annotation { "Feature Type Name" : "Feature", "Feature Type Description" : "" }
export const myFeature = defineFeature(function(context is Context, id is Id, definition is map)
    precondition{}
    {
        {
            var Q0;
            Q0=qCreatedBy(makeId("Top.planeOp"),FACE);
            var sketch = newSketch(context, id + "F0", { "sketchPlane" : qUnion([Q0])});
            skLineSegment(sketch, "E0.bottom", {"start": v(-43.83, 34.62) * mm, "end": v(22.17, 34.62) * mm});
            skLineSegment(sketch, "E0.top", {"start": v(-42.5, -18.38) * mm, "end": v(22.17, -18.38) * mm});
            skLineSegment(sketch, "E0.left", {"start": v(-43.83, 34.62) * mm, "end": v(-43.83, 32.11) * mm});
            skLineSegment(sketch, "E0.right", {"start": v(22.17, 34.62) * mm, "end": v(22.17, -18.38) * mm});
            skLineSegment(sketch, "E1", {"start": v(-43.83, -16.89) * mm, "end": v(-42.5, -18.38) * mm});
            skLineSegment(sketch, "E2.right", {"start": v(-46.83, 29.1) * mm, "end": v(-46.73, -3) * mm});
            skLineSegment(sketch, "E3", {"start": v(-43.83, 32.11) * mm, "end": v(-46.83, 29.1) * mm});
            skLineSegment(sketch, "E4", {"start": v(-46.73, -3) * mm, "end": v(-43.83, -5.89) * mm});
            skLineSegment(sketch, "E5.trimOffspring", {"start": v(-43.83, -5.89) * mm, "end": v(-43.83, -16.89) * mm});
            skCircle(sketch, "E6", {"center": v(-44.33, 27.39) * mm, "radius": 2.25 * mm});
            skCircle(sketch, "E7", {"center": v(-44.24, -1.2) * mm, "radius": 2.25 * mm});
            skCircle(sketch, "E8", {"center": v(6.92, 32.12) * mm, "radius": 2.25 * mm});
            skCircle(sketch, "E9", {"center": v(6.92, -15.88) * mm, "radius": 2.25 * mm});
            skSolve(sketch);
        }
        {
            var Q0;
            Q0=makeQuery(id+"F0.imprint","IMPRINT",FACE,{"disambiguationData":[TD([[makeQuery(id+"F0.imprint","IMPRINT",EDGE,{"derivedFrom":sQuery(id+"F0.wireOp",EDGE,"E0.bottom")}),-1.0]])]});
            var Q1;
            Q1=makeQuery(id+"F0.imprint","IMPRINT",FACE,{"disambiguationData":[TD([[makeQuery(id+"F0.imprint","IMPRINT",EDGE,{"derivedFrom":sQuery(id+"F0.wireOp",EDGE,"oReomVxt-EG6t-q1BH-AZSM-6wqQi52AqEO8")}),-1.0]])]});
            extrude(context, id + "F1", {"entities" : qUnion([Q0, Q1]), "depth" : 1 * mm});
        }
        {
            var Q0;
            Q0=makeQuery(id+"F1.opExtrude","CAP_FACE",FACE,{"disambiguationData":[OSD([sQuery(id+"F0.wireOp",EDGE,"E0.bottom"),sQuery(id+"F0.wireOp",EDGE,"E0.top"),sQuery(id+"F0.wireOp",EDGE,"E0.left"),sQuery(id+"F0.wireOp",EDGE,"E0.right"),sQuery(id+"F0.wireOp",EDGE,"E1"),sQuery(id+"F0.wireOp",EDGE,"E2.right"),sQuery(id+"F0.wireOp",EDGE,"E3"),sQuery(id+"F0.wireOp",EDGE,"E4"),sQuery(id+"F0.wireOp",EDGE,"E5.trimOffspring"),sQuery(id+"F0.wireOp",EDGE,"E6"),sQuery(id+"F0.wireOp",EDGE,"E7"),sQuery(id+"F0.wireOp",EDGE,"E8"),sQuery(id+"F0.wireOp",EDGE,"E9")])],"isStart":true});
            var sketch = newSketch(context, id + "F2", { "sketchPlane" : qUnion([Q0])});
            skText(sketch, "E10", { "text": "Seonwoo Cho\nJulia Angel", "fontName": "OpenSans-Regular.ttf"});
            const initialGuessF2  = {"E10": [-0.03303, 0.00577, 1, 0, 0.006]};
            skSetInitialGuess(sketch, initialGuessF2);
            skSolve(sketch);
        }
        {
            var Q0;
            Q0=qSketchRegion(id+"F2",true);
            extrude(context, id + "F3", {"entities" : qUnion([Q0]), "operationType" : NewBodyOperationType.REMOVE, "oppositeDirection" : true, "depth" : 0.01 * mm});
        }
        {
            var Q0;
            Q0=makeQuery(id+"F1.opExtrude","CAP_FACE",FACE,{"disambiguationData":[OSD([sQuery(id+"F0.wireOp",EDGE,"E0.bottom"),sQuery(id+"F0.wireOp",EDGE,"E0.top"),sQuery(id+"F0.wireOp",EDGE,"E0.left"),sQuery(id+"F0.wireOp",EDGE,"E0.right"),sQuery(id+"F0.wireOp",EDGE,"E1"),sQuery(id+"F0.wireOp",EDGE,"E2.right"),sQuery(id+"F0.wireOp",EDGE,"E3"),sQuery(id+"F0.wireOp",EDGE,"E4"),sQuery(id+"F0.wireOp",EDGE,"E5.trimOffspring"),sQuery(id+"F0.wireOp",EDGE,"E6"),sQuery(id+"F0.wireOp",EDGE,"E7"),sQuery(id+"F0.wireOp",EDGE,"E8"),sQuery(id+"F0.wireOp",EDGE,"E9")])],"isStart":false});
            var sketch = newSketch(context, id + "F4", { "sketchPlane" : qUnion([Q0])});
            skLineSegment(sketch, "E11.bottom", {"start": v(17.67, -3.38) * mm, "end": v(25.67, -3.38) * mm});
            skLineSegment(sketch, "E11.top", {"start": v(17.67, -10.38) * mm, "end": v(25.67, -10.38) * mm});
            skLineSegment(sketch, "E11.left", {"start": v(17.67, -3.38) * mm, "end": v(17.67, -10.38) * mm});
            skLineSegment(sketch, "E11.right", {"start": v(25.67, -3.38) * mm, "end": v(25.67, -10.38) * mm});
            skSolve(sketch);
        }
        {
            var Q0;
            {var subQ0=sQuery(id+"F4.wireOp",EDGE,"E11.right");Q0=makeQuery(id+"F4.imprint","IMPRINT",FACE,{"disambiguationData":[TD([[makeQuery(id+"F4.imprint","IMPRINT",EDGE,{"derivedFrom":subQ0}),-1.0]])]});}
            var Q1;
            {var subQ0=sQuery(id+"F4.wireOp",EDGE,"E11.left");Q1=makeQuery(id+"F4.imprint","IMPRINT",FACE,{"disambiguationData":[TD([[makeQuery(id+"F4.imprint","IMPRINT",EDGE,{"derivedFrom":subQ0}),1.0]])]});}
            extrude(context, id + "F5", {"entities" : qUnion([Q0, Q1]), "operationType" : NewBodyOperationType.ADD, "depth" : 4 * mm});
        }
        {
            var Q0;
            Q0=makeQuery(id+"F5.opExtrude","SWEPT_FACE",FACE,{"disambiguationData":[OSD([sQuery(id+"F4.wireOp",EDGE,"E11.right")])]});
            var sketch = newSketch(context, id + "F6", { "sketchPlane" : qUnion([Q0])});
            skLineSegment(sketch, "E12", {"start": v(-10.38, 3) * mm, "end": v(-10.11, 2.75) * mm});
            skLineSegment(sketch, "E13", {"start": v(-10.08, 2.67) * mm, "end": v(-10.08, 1) * mm});
            skLineSegment(sketch, "E14", {"start": v(-3.38, 3) * mm, "end": v(-3.65, 2.75) * mm});
            skLineSegment(sketch, "E15", {"start": v(-3.68, 2.68) * mm, "end": v(-3.68, 1) * mm});
            skPoint(sketch, "E16.visualSharp", {"position": v(-3.68, 2.72) * mm});
            skArc(sketch, "E16.filletArc", {"start": v(-3.65, 2.75) * mm, "mid": v(-3.67, 2.72) * mm, "end": v(-3.68, 2.68) * mm});
            skPoint(sketch, "E17.visualSharp", {"position": v(-10.08, 2.72) * mm});
            skArc(sketch, "E17.filletArc", {"start": v(-10.08, 2.67) * mm, "mid": v(-10.09, 2.71) * mm, "end": v(-10.11, 2.75) * mm});
            skArc(sketch, "E18", {"start": v(-10.17, 5) * mm, "mid": v(-10.33, 4.94) * mm, "end": v(-10.38, 4.77) * mm});
            skArc(sketch, "E19", {"start": v(-3.38, 4.86) * mm, "mid": v(-3.44, 4.95) * mm, "end": v(-3.54, 5) * mm});
            skArc(sketch, "E20", {"start": v(-10.08, 1.19) * mm, "mid": v(-10.05, 1.08) * mm, "end": v(-9.98, 1) * mm});
            skArc(sketch, "E21", {"start": v(-3.85, 1) * mm, "mid": v(-3.74, 1.05) * mm, "end": v(-3.68, 1.17) * mm});
            skArc(sketch, "E22", {"start": v(-10.38, 3.04) * mm, "mid": v(-10.38, 3.01) * mm, "end": v(-10.36, 2.98) * mm});
            skArc(sketch, "E23", {"start": v(-3.48, 2.91) * mm, "mid": v(-3.37, 3.02) * mm, "end": v(-3.38, 3.18) * mm});
            skLineSegment(sketch, "E24", {"start": v(-10.08, 4.8) * mm, "end": v(-3.72, 4.8) * mm});
            skLineSegment(sketch, "E25", {"start": v(-3.58, 4.66) * mm, "end": v(-3.57, 3.17) * mm});
            skLineSegment(sketch, "E26", {"start": v(-3.87, 2.75) * mm, "end": v(-3.62, 3.04) * mm});
            skLineSegment(sketch, "E27", {"start": v(-3.87, 1.33) * mm, "end": v(-3.87, 2.75) * mm});
            skLineSegment(sketch, "E28", {"start": v(-10.19, 4.7) * mm, "end": v(-10.19, 3.14) * mm});
            skLineSegment(sketch, "E29", {"start": v(-9.9, 2.75) * mm, "end": v(-9.88, 1.26) * mm});
            skLineSegment(sketch, "E30", {"start": v(-4, 1.19) * mm, "end": v(-9.78, 1.18) * mm});
            skLineSegment(sketch, "E31", {"start": v(-10.13, 2.98) * mm, "end": v(-9.9, 2.75) * mm});
            skArc(sketch, "E32", {"start": v(-3.58, 4.66) * mm, "mid": v(-3.63, 4.75) * mm, "end": v(-3.72, 4.8) * mm});
            skArc(sketch, "E33", {"start": v(-10.08, 4.8) * mm, "mid": v(-10.15, 4.77) * mm, "end": v(-10.19, 4.7) * mm});
            skArc(sketch, "E34", {"start": v(-10.19, 3.14) * mm, "mid": v(-10.17, 3.06) * mm, "end": v(-10.13, 2.98) * mm});
            skArc(sketch, "E35", {"start": v(-9.88, 1.3) * mm, "mid": v(-9.85, 1.21) * mm, "end": v(-9.78, 1.18) * mm});
            skArc(sketch, "E36", {"start": v(-4, 1.19) * mm, "mid": v(-3.9, 1.23) * mm, "end": v(-3.87, 1.33) * mm});
            skArc(sketch, "E37", {"start": v(-3.62, 3.04) * mm, "mid": v(-3.58, 3.1) * mm, "end": v(-3.57, 3.17) * mm});
            skPoint(sketch, "E38.orphan", {"position": v(-10.19, 3.04) * mm});
            skSolve(sketch);
        }
        {
            var Q0;
            {var subQ0=sQuery(id+"F6.wireOp",EDGE,"E14");Q0=makeQuery(id+"F6.imprint","IMPRINT",FACE,{"disambiguationData":[TD([[makeQuery(id+"F6.imprint","IMPRINT",EDGE,{"derivedFrom":subQ0}),1.0]])]});}
            extrude(context, id + "F7", {"entities" : qUnion([Q0]), "operationType" : NewBodyOperationType.REMOVE, "oppositeDirection" : true, "depth" : 25.4 * mm});
        }
        {
            var Q0;
            {var subQ0=sQuery(id+"F6.wireOp",EDGE,"E12");Q0=makeQuery(id+"F6.imprint","IMPRINT",FACE,{"disambiguationData":[TD([[makeQuery(id+"F6.imprint","IMPRINT",EDGE,{"derivedFrom":subQ0}),-1.0]])]});}
            extrude(context, id + "F8", {"entities" : qUnion([Q0]), "operationType" : NewBodyOperationType.REMOVE, "oppositeDirection" : true, "depth" : 25.4 * mm});
        }
        {
            var Q0;
            {var subQ0=sQuery(id+"F4.wireOp",EDGE,"E11.left");Q0=makeQuery(id+"F4.imprint","IMPRINT",FACE,{"disambiguationData":[TD([[makeQuery(id+"F4.imprint","IMPRINT",EDGE,{"derivedFrom":subQ0}),-1.0]])]});}
            var sketch = newSketch(context, id + "F9", { "sketchPlane" : qUnion([Q0])});
            skLineSegment(sketch, "E39", {"start": v(21.67, -10.38) * mm, "end": v(21.67, -3.38) * mm});
            skLineSegment(sketch, "E40", {"start": v(21.67, -3.38) * mm, "end": v(25.67, -3.38) * mm});
            skLineSegment(sketch, "E41", {"start": v(21.67, -10.38) * mm, "end": v(25.67, -10.38) * mm});
            skLineSegment(sketch, "E42.bottom", {"start": v(-42.83, 33.62) * mm, "end": v(-27.33, 33.62) * mm});
            skLineSegment(sketch, "E42.top", {"start": v(-42.83, 31.62) * mm, "end": v(-27.33, 31.62) * mm});
            skLineSegment(sketch, "E42.left", {"start": v(-42.83, 33.62) * mm, "end": v(-42.83, 31.62) * mm});
            skLineSegment(sketch, "E42.right", {"start": v(-27.33, 33.62) * mm, "end": v(-27.33, 31.62) * mm});
            skLineSegment(sketch, "E43.bottom", {"start": v(-25.33, 33.62) * mm, "end": v(-9.83, 33.62) * mm});
            skLineSegment(sketch, "E43.top", {"start": v(-25.33, 31.62) * mm, "end": v(-9.83, 31.62) * mm});
            skLineSegment(sketch, "E43.left", {"start": v(-25.33, 33.62) * mm, "end": v(-25.33, 31.62) * mm});
            skLineSegment(sketch, "E43.right", {"start": v(-9.83, 33.62) * mm, "end": v(-9.83, 31.62) * mm});
            skLineSegment(sketch, "E44.bottom", {"start": v(-42.83, -15.38) * mm, "end": v(-22.33, -15.38) * mm});
            skLineSegment(sketch, "E44.top", {"start": v(-42.83, -17.38) * mm, "end": v(-22.33, -17.38) * mm});
            skLineSegment(sketch, "E44.left", {"start": v(-42.83, -15.38) * mm, "end": v(-42.83, -17.38) * mm});
            skLineSegment(sketch, "E44.right", {"start": v(-22.33, -15.38) * mm, "end": v(-22.33, -17.38) * mm});
            skLineSegment(sketch, "E45.bottom", {"start": v(-20.33, -15.38) * mm, "end": v(0.17, -15.38) * mm});
            skLineSegment(sketch, "E45.top", {"start": v(-20.33, -17.38) * mm, "end": v(0.17, -17.38) * mm});
            skLineSegment(sketch, "E45.left", {"start": v(-20.33, -15.38) * mm, "end": v(-20.33, -17.38) * mm});
            skLineSegment(sketch, "E45.right", {"start": v(0.17, -15.38) * mm, "end": v(0.17, -17.38) * mm});
            skSolve(sketch);
        }
        {
            var Q0;
            {var subQ0=sQuery(id+"F6.wireOp",EDGE,"E19");var subQ1=sQuery(id+"F4.wireOp",EDGE,"E11.right");var subQ4=makeQuery(id+"F5.opExtrude","CAP_EDGE",EDGE,{"disambiguationData":[OSD([subQ1])],"isStart":false});var subQ5=makeQuery(id+"F6.imprint","INTERSECT",VERTEX,{"disambiguationData":[OD(1.0)],"derivedFrom":[subQ4,subQ0]});Q0=makeQuery(id+"F6.imprint","IMPRINT",FACE,{"disambiguationData":[TD([[makeQuery(id+"F6.imprint","IMPRINT",EDGE,{"disambiguationData":[TD([[subQ5,1.0]])],"derivedFrom":subQ0}),-1.0]])]});}
            extrude(context, id + "F10", {"entities" : qUnion([Q0]), "operationType" : NewBodyOperationType.REMOVE, "oppositeDirection" : true, "depth" : 25.4 * mm});
        }
        {
            var Q0;
            {var subQ3=sQuery(id+"F6.wireOp",EDGE,"E21");Q0=makeQuery(id+"F6.imprint","IMPRINT",FACE,{"disambiguationData":[TD([[makeQuery(id+"F6.imprint","IMPRINT",EDGE,{"derivedFrom":subQ3}),-1.0]])]});}
            extrude(context, id + "F11", {"entities" : qUnion([Q0]), "operationType" : NewBodyOperationType.REMOVE, "oppositeDirection" : true, "depth" : 25.4 * mm});
        }
        {
            var Q0;
            {var subQ3=sQuery(id+"F6.wireOp",EDGE,"E20");Q0=makeQuery(id+"F6.imprint","IMPRINT",FACE,{"disambiguationData":[TD([[makeQuery(id+"F6.imprint","IMPRINT",EDGE,{"derivedFrom":subQ3}),-1.0]])]});}
            extrude(context, id + "F12", {"entities" : qUnion([Q0]), "operationType" : NewBodyOperationType.REMOVE, "oppositeDirection" : true, "depth" : 25.4 * mm});
        }
        {
            var Q0;
            {var subQ0=sQuery(id+"F6.wireOp",EDGE,"E18");var subQ1=sQuery(id+"F4.wireOp",EDGE,"E11.right");var subQ2=makeQuery(id+"F5.opExtrude","CAP_EDGE",EDGE,{"disambiguationData":[OSD([subQ1])],"isStart":false});var subQ3=makeQuery(id+"F6.imprint","INTERSECT",VERTEX,{"disambiguationData":[OD(1.0)],"derivedFrom":[subQ2,subQ0]});Q0=makeQuery(id+"F6.imprint","IMPRINT",FACE,{"disambiguationData":[TD([[makeQuery(id+"F6.imprint","IMPRINT",EDGE,{"disambiguationData":[TD([[subQ3,-1.0]])],"derivedFrom":subQ0}),-1.0]])]});}
            extrude(context, id + "F13", {"entities" : qUnion([Q0]), "operationType" : NewBodyOperationType.REMOVE, "oppositeDirection" : true, "depth" : 25.4 * mm});
        }
        {
            var Q0;
            {var subQ0=sQuery(id+"F6.wireOp",EDGE,"E14");var subQ3=sQuery(id+"F6.wireOp",EDGE,"E23");var subQ4=makeQuery(id+"F6.imprint","INTERSECT",VERTEX,{"derivedFrom":[subQ0,subQ3]});Q0=makeQuery(id+"F6.imprint","IMPRINT",FACE,{"disambiguationData":[TD([[makeQuery(id+"F6.imprint","IMPRINT",EDGE,{"disambiguationData":[TD([[subQ4,1.0]])],"derivedFrom":subQ0}),-1.0]])]});}
            extrude(context, id + "F14", {"entities" : qUnion([Q0]), "operationType" : NewBodyOperationType.REMOVE, "oppositeDirection" : true, "depth" : 25.4 * mm});
        }
        {
            var Q0;
            {var subQ0=sQuery(id+"F6.wireOp",EDGE,"E12");var subQ3=sQuery(id+"F6.wireOp",EDGE,"E22");var subQ4=makeQuery(id+"F6.imprint","INTERSECT",VERTEX,{"derivedFrom":[subQ0,subQ3]});Q0=makeQuery(id+"F6.imprint","IMPRINT",FACE,{"disambiguationData":[TD([[makeQuery(id+"F6.imprint","IMPRINT",EDGE,{"disambiguationData":[TD([[subQ4,1.0]])],"derivedFrom":subQ0}),1.0]])]});}
            extrude(context, id + "F15", {"entities" : qUnion([Q0]), "operationType" : NewBodyOperationType.REMOVE, "oppositeDirection" : true, "depth" : 25.4 * mm});
        }
        {
            var Q0;
            Q0=makeQuery(id+"F6.imprint","IMPRINT",FACE,{"disambiguationData":[TD([[makeQuery(id+"F6.imprint","IMPRINT",EDGE,{"derivedFrom":sQuery(id+"F6.wireOp",EDGE,"E24")}),-1.0]])]});
            extrude(context, id + "F16", {"entities" : qUnion([Q0]), "operationType" : NewBodyOperationType.ADD, "oppositeDirection" : true, "depth" : 7.5 * mm});
        }
        {
            var Q0;
            Q0=makeQuery(id+"F6.imprint","IMPRINT",FACE,{"disambiguationData":[TD([[makeQuery(id+"F6.imprint","IMPRINT",EDGE,{"derivedFrom":sQuery(id+"F6.wireOp",EDGE,"E24")}),-1.0]])]});
            extrude(context, id + "F17", {"entities" : qUnion([Q0]), "operationType" : NewBodyOperationType.REMOVE, "oppositeDirection" : true, "depth" : 7.5 * mm});
        }
        {
            var Q0;
            Q0=makeQuery(id+"F9.imprint","IMPRINT",FACE,{"disambiguationData":[TD([[makeQuery(id+"F9.imprint","IMPRINT",EDGE,{"derivedFrom":sQuery(id+"F9.wireOp",EDGE,"E42.bottom")}),-1.0]])]});
            extrude(context, id + "F18", {"entities" : qUnion([Q0]), "operationType" : NewBodyOperationType.ADD, "depth" : 9 * mm});
        }
        {
            var Q0;
            Q0=makeQuery(id+"F9.imprint","IMPRINT",FACE,{"disambiguationData":[TD([[makeQuery(id+"F9.imprint","IMPRINT",EDGE,{"derivedFrom":sQuery(id+"F9.wireOp",EDGE,"E43.bottom")}),-1.0]])]});
            var Q1;
            Q1=makeQuery(id+"F9.imprint","IMPRINT",FACE,{"disambiguationData":[TD([[makeQuery(id+"F9.imprint","IMPRINT",EDGE,{"derivedFrom":sQuery(id+"F9.wireOp",EDGE,"E44.bottom")}),-1.0]])]});
            var Q2;
            Q2=makeQuery(id+"F9.imprint","IMPRINT",FACE,{"disambiguationData":[TD([[makeQuery(id+"F9.imprint","IMPRINT",EDGE,{"derivedFrom":sQuery(id+"F9.wireOp",EDGE,"E45.bottom")}),-1.0]])]});
            extrude(context, id + "F19", {"entities" : qUnion([Q0, Q1, Q2]), "operationType" : NewBodyOperationType.ADD, "depth" : 9 * mm});
        }
        {
            var Q0;
            Q0=makeQuery(id+"F18.opExtrude","CAP_FACE",FACE,{"disambiguationData":[OSD([sQuery(id+"F9.wireOp",EDGE,"E42.bottom"),sQuery(id+"F9.wireOp",EDGE,"E42.top"),sQuery(id+"F9.wireOp",EDGE,"E42.left"),sQuery(id+"F9.wireOp",EDGE,"E42.right")])],"isStart":false});
            var sketch = newSketch(context, id + "F20", { "sketchPlane" : qUnion([Q0])});
            skLineSegment(sketch, "E46.bottom", {"start": v(-42.03, 33.25) * mm, "end": v(-40.73, 33.25) * mm});
            skLineSegment(sketch, "E46.top", {"start": v(-42.03, 31.95) * mm, "end": v(-40.73, 31.95) * mm});
            skLineSegment(sketch, "E46.left", {"start": v(-42.03, 33.25) * mm, "end": v(-42.03, 31.95) * mm});
            skLineSegment(sketch, "E46.right", {"start": v(-40.73, 33.25) * mm, "end": v(-40.73, 31.95) * mm});
            skLineSegment(sketch, "E47.1.0.0", {"start": v(-39.53, 33.25) * mm, "end": v(-39.53, 31.95) * mm});
            skLineSegment(sketch, "E47.1.0.1", {"start": v(-39.53, 33.25) * mm, "end": v(-38.23, 33.25) * mm});
            skLineSegment(sketch, "E47.1.0.2", {"start": v(-38.23, 33.25) * mm, "end": v(-38.23, 31.95) * mm});
            skLineSegment(sketch, "E47.1.0.3", {"start": v(-39.53, 31.95) * mm, "end": v(-38.23, 31.95) * mm});
            skLineSegment(sketch, "E47.2.0.0", {"start": v(-37.03, 33.25) * mm, "end": v(-37.03, 31.95) * mm});
            skLineSegment(sketch, "E47.2.0.1", {"start": v(-37.03, 33.25) * mm, "end": v(-35.73, 33.25) * mm});
            skLineSegment(sketch, "E47.2.0.2", {"start": v(-35.73, 33.25) * mm, "end": v(-35.73, 31.95) * mm});
            skLineSegment(sketch, "E47.2.0.3", {"start": v(-37.03, 31.95) * mm, "end": v(-35.73, 31.95) * mm});
            skLineSegment(sketch, "E47.direction1", {"start": v(-42.03, 31.95) * mm, "end": v(-39.53, 31.95) * mm, "construction": true});
            skLineSegment(sketch, "E48.0.3.0", {"start": v(-34.53, 33.25) * mm, "end": v(-34.53, 31.95) * mm});
            skLineSegment(sketch, "E48.3.3.0", {"start": v(-34.53, 33.25) * mm, "end": v(-33.23, 33.25) * mm});
            skLineSegment(sketch, "E48.6.3.0", {"start": v(-33.23, 33.25) * mm, "end": v(-33.23, 31.95) * mm});
            skLineSegment(sketch, "E48.9.3.0", {"start": v(-34.53, 31.95) * mm, "end": v(-33.23, 31.95) * mm});
            skLineSegment(sketch, "E48.0.4.0", {"start": v(-32.03, 33.25) * mm, "end": v(-32.03, 31.95) * mm});
            skLineSegment(sketch, "E48.3.4.0", {"start": v(-32.03, 33.25) * mm, "end": v(-30.73, 33.25) * mm});
            skLineSegment(sketch, "E48.6.4.0", {"start": v(-30.73, 33.25) * mm, "end": v(-30.73, 31.95) * mm});
            skLineSegment(sketch, "E48.9.4.0", {"start": v(-32.03, 31.95) * mm, "end": v(-30.73, 31.95) * mm});
            skLineSegment(sketch, "E48.0.5.0", {"start": v(-29.53, 33.25) * mm, "end": v(-29.53, 31.95) * mm});
            skLineSegment(sketch, "E48.3.5.0", {"start": v(-29.53, 33.25) * mm, "end": v(-28.23, 33.25) * mm});
            skLineSegment(sketch, "E48.6.5.0", {"start": v(-28.23, 33.25) * mm, "end": v(-28.23, 31.95) * mm});
            skLineSegment(sketch, "E48.9.5.0", {"start": v(-29.53, 31.95) * mm, "end": v(-28.23, 31.95) * mm});
            skSolve(sketch);
        }
        {
            var Q0;
            Q0=makeQuery(id+"F20.imprint","IMPRINT",FACE,{"disambiguationData":[TD([[makeQuery(id+"F20.imprint","IMPRINT",EDGE,{"derivedFrom":sQuery(id+"F20.wireOp",EDGE,"E46.bottom")}),-1.0]])]});
            var Q1;
            Q1=makeQuery(id+"F20.imprint","IMPRINT",FACE,{"disambiguationData":[TD([[makeQuery(id+"F20.imprint","IMPRINT",EDGE,{"derivedFrom":sQuery(id+"F20.wireOp",EDGE,"E47.1.0.0")}),1.0]])]});
            var Q2;
            Q2=makeQuery(id+"F20.imprint","IMPRINT",FACE,{"disambiguationData":[TD([[makeQuery(id+"F20.imprint","IMPRINT",EDGE,{"derivedFrom":sQuery(id+"F20.wireOp",EDGE,"E47.2.0.0")}),1.0]])]});
            var Q3;
            Q3=makeQuery(id+"F20.imprint","IMPRINT",FACE,{"disambiguationData":[TD([[makeQuery(id+"F20.imprint","IMPRINT",EDGE,{"derivedFrom":sQuery(id+"F20.wireOp",EDGE,"E48.0.3.0")}),1.0]])]});
            var Q4;
            Q4=makeQuery(id+"F20.imprint","IMPRINT",FACE,{"disambiguationData":[TD([[makeQuery(id+"F20.imprint","IMPRINT",EDGE,{"derivedFrom":sQuery(id+"F20.wireOp",EDGE,"E48.0.4.0")}),1.0]])]});
            var Q5;
            Q5=makeQuery(id+"F20.imprint","IMPRINT",FACE,{"disambiguationData":[TD([[makeQuery(id+"F20.imprint","IMPRINT",EDGE,{"derivedFrom":sQuery(id+"F20.wireOp",EDGE,"E48.0.5.0")}),1.0]])]});
            extrude(context, id + "F21", {"entities" : qUnion([Q0, Q1, Q2, Q3, Q4, Q5]), "operationType" : NewBodyOperationType.REMOVE, "oppositeDirection" : true, "depth" : 8 * mm});
        }
        {
            var Q0;
            Q0=makeQuery(id+"F19.opExtrude","CAP_FACE",FACE,{"disambiguationData":[OSD([sQuery(id+"F9.wireOp",EDGE,"E45.bottom"),sQuery(id+"F9.wireOp",EDGE,"E45.top"),sQuery(id+"F9.wireOp",EDGE,"E45.left"),sQuery(id+"F9.wireOp",EDGE,"E45.right")])],"isStart":false});
            var sketch = newSketch(context, id + "F22", { "sketchPlane" : qUnion([Q0])});
            skLineSegment(sketch, "E49.bottom", {"start": v(-19.53, -15.78) * mm, "end": v(-18.23, -15.78) * mm});
            skLineSegment(sketch, "E49.top", {"start": v(-19.53, -17.08) * mm, "end": v(-18.23, -17.08) * mm});
            skLineSegment(sketch, "E49.left", {"start": v(-19.53, -15.78) * mm, "end": v(-19.53, -17.08) * mm});
            skLineSegment(sketch, "E49.right", {"start": v(-18.23, -15.78) * mm, "end": v(-18.23, -17.08) * mm});
            skLineSegment(sketch, "E50.1.0.0", {"start": v(-15.74, -15.78) * mm, "end": v(-15.74, -17.08) * mm});
            skLineSegment(sketch, "E50.1.0.1", {"start": v(-17.04, -15.78) * mm, "end": v(-15.74, -15.78) * mm});
            skLineSegment(sketch, "E50.1.0.2", {"start": v(-17.04, -17.08) * mm, "end": v(-15.74, -17.08) * mm});
            skLineSegment(sketch, "E50.1.0.3", {"start": v(-17.04, -15.78) * mm, "end": v(-17.04, -17.08) * mm});
            skLineSegment(sketch, "E50.2.0.0", {"start": v(-13.25, -15.78) * mm, "end": v(-13.25, -17.08) * mm});
            skLineSegment(sketch, "E50.2.0.1", {"start": v(-14.55, -15.78) * mm, "end": v(-13.25, -15.78) * mm});
            skLineSegment(sketch, "E50.2.0.2", {"start": v(-14.55, -17.08) * mm, "end": v(-13.25, -17.08) * mm});
            skLineSegment(sketch, "E50.2.0.3", {"start": v(-14.55, -15.78) * mm, "end": v(-14.55, -17.08) * mm});
            skLineSegment(sketch, "E50.3.0.0", {"start": v(-10.76, -15.78) * mm, "end": v(-10.76, -17.08) * mm});
            skLineSegment(sketch, "E50.3.0.1", {"start": v(-12.06, -15.78) * mm, "end": v(-10.76, -15.78) * mm});
            skLineSegment(sketch, "E50.3.0.2", {"start": v(-12.06, -17.08) * mm, "end": v(-10.76, -17.08) * mm});
            skLineSegment(sketch, "E50.3.0.3", {"start": v(-12.06, -15.78) * mm, "end": v(-12.06, -17.08) * mm});
            skLineSegment(sketch, "E50.4.0.0", {"start": v(-8.27, -15.78) * mm, "end": v(-8.27, -17.08) * mm});
            skLineSegment(sketch, "E50.4.0.1", {"start": v(-9.57, -15.78) * mm, "end": v(-8.27, -15.78) * mm});
            skLineSegment(sketch, "E50.4.0.2", {"start": v(-9.57, -17.08) * mm, "end": v(-8.27, -17.08) * mm});
            skLineSegment(sketch, "E50.4.0.3", {"start": v(-9.57, -15.78) * mm, "end": v(-9.57, -17.08) * mm});
            skLineSegment(sketch, "E50.5.0.0", {"start": v(-5.79, -15.78) * mm, "end": v(-5.79, -17.08) * mm});
            skLineSegment(sketch, "E50.5.0.1", {"start": v(-7.09, -15.78) * mm, "end": v(-5.79, -15.78) * mm});
            skLineSegment(sketch, "E50.5.0.2", {"start": v(-7.09, -17.08) * mm, "end": v(-5.79, -17.08) * mm});
            skLineSegment(sketch, "E50.5.0.3", {"start": v(-7.09, -15.78) * mm, "end": v(-7.09, -17.08) * mm});
            skLineSegment(sketch, "E50.6.0.0", {"start": v(-3.3, -15.78) * mm, "end": v(-3.3, -17.08) * mm});
            skLineSegment(sketch, "E50.6.0.1", {"start": v(-4.6, -15.78) * mm, "end": v(-3.3, -15.78) * mm});
            skLineSegment(sketch, "E50.6.0.2", {"start": v(-4.6, -17.08) * mm, "end": v(-3.3, -17.08) * mm});
            skLineSegment(sketch, "E50.6.0.3", {"start": v(-4.6, -15.78) * mm, "end": v(-4.6, -17.08) * mm});
            skLineSegment(sketch, "E50.7.0.0", {"start": v(-0.8, -15.78) * mm, "end": v(-0.8, -17.08) * mm});
            skLineSegment(sketch, "E50.7.0.1", {"start": v(-2.1, -15.78) * mm, "end": v(-0.8, -15.78) * mm});
            skLineSegment(sketch, "E50.7.0.2", {"start": v(-2.1, -17.08) * mm, "end": v(-0.8, -17.08) * mm});
            skLineSegment(sketch, "E50.7.0.3", {"start": v(-2.1, -15.78) * mm, "end": v(-2.1, -17.08) * mm});
            skLineSegment(sketch, "E50.direction1", {"start": v(-18.23, -17.08) * mm, "end": v(-15.74, -17.08) * mm, "construction": true});
            skSolve(sketch);
        }
        {
            var Q0;
            Q0=makeQuery(id+"F22.imprint","IMPRINT",FACE,{"disambiguationData":[TD([[makeQuery(id+"F22.imprint","IMPRINT",EDGE,{"derivedFrom":sQuery(id+"F22.wireOp",EDGE,"E49.bottom")}),-1.0]])]});
            var Q1;
            Q1=makeQuery(id+"F22.imprint","IMPRINT",FACE,{"disambiguationData":[TD([[makeQuery(id+"F22.imprint","IMPRINT",EDGE,{"derivedFrom":sQuery(id+"F22.wireOp",EDGE,"E50.1.0.0")}),-1.0]])]});
            var Q2;
            Q2=makeQuery(id+"F22.imprint","IMPRINT",FACE,{"disambiguationData":[TD([[makeQuery(id+"F22.imprint","IMPRINT",EDGE,{"derivedFrom":sQuery(id+"F22.wireOp",EDGE,"E50.2.0.0")}),-1.0]])]});
            var Q3;
            Q3=makeQuery(id+"F22.imprint","IMPRINT",FACE,{"disambiguationData":[TD([[makeQuery(id+"F22.imprint","IMPRINT",EDGE,{"derivedFrom":sQuery(id+"F22.wireOp",EDGE,"E50.3.0.0")}),-1.0]])]});
            var Q4;
            Q4=makeQuery(id+"F22.imprint","IMPRINT",FACE,{"disambiguationData":[TD([[makeQuery(id+"F22.imprint","IMPRINT",EDGE,{"derivedFrom":sQuery(id+"F22.wireOp",EDGE,"E50.4.0.0")}),-1.0]])]});
            var Q5;
            Q5=makeQuery(id+"F22.imprint","IMPRINT",FACE,{"disambiguationData":[TD([[makeQuery(id+"F22.imprint","IMPRINT",EDGE,{"derivedFrom":sQuery(id+"F22.wireOp",EDGE,"E50.5.0.0")}),-1.0]])]});
            var Q6;
            Q6=makeQuery(id+"F22.imprint","IMPRINT",FACE,{"disambiguationData":[TD([[makeQuery(id+"F22.imprint","IMPRINT",EDGE,{"derivedFrom":sQuery(id+"F22.wireOp",EDGE,"E50.6.0.0")}),-1.0]])]});
            var Q7;
            Q7=makeQuery(id+"F22.imprint","IMPRINT",FACE,{"disambiguationData":[TD([[makeQuery(id+"F22.imprint","IMPRINT",EDGE,{"derivedFrom":sQuery(id+"F22.wireOp",EDGE,"E50.7.0.0")}),-1.0]])]});
            extrude(context, id + "F23", {"entities" : qUnion([Q0, Q1, Q2, Q3, Q4, Q5, Q6, Q7]), "operationType" : NewBodyOperationType.REMOVE, "oppositeDirection" : true, "depth" : 8 * mm});
        }
        {
            var Q0;
            {var subQ0=sQuery(id+"F4.wireOp",EDGE,"E11.left");Q0=makeQuery(id+"F4.imprint","IMPRINT",FACE,{"disambiguationData":[TD([[makeQuery(id+"F4.imprint","IMPRINT",EDGE,{"derivedFrom":subQ0}),-1.0]])]});}
            var sketch = newSketch(context, id + "F24", { "sketchPlane" : qUnion([Q0])});
            skLineSegment(sketch, "E51.bottom", {"start": v(-9.23, 32.62) * mm, "end": v(-3.23, 32.62) * mm});
            skLineSegment(sketch, "E51.top", {"start": v(-8.05, 26.62) * mm, "end": v(-4.42, 26.62) * mm});
            skLineSegment(sketch, "E51.left", {"start": v(-9.23, 32.62) * mm, "end": v(-9.23, 27.72) * mm});
            skLineSegment(sketch, "E51.right", {"start": v(-3.23, 32.62) * mm, "end": v(-3.23, 27.72) * mm});
            skLineSegment(sketch, "E52.bottom", {"start": v(-3.03, 32.62) * mm, "end": v(2.97, 32.62) * mm});
            skLineSegment(sketch, "E52.top", {"start": v(-2.01, 26.62) * mm, "end": v(1.95, 26.62) * mm});
            skLineSegment(sketch, "E52.left", {"start": v(-3.03, 32.62) * mm, "end": v(-3.03, 27.72) * mm});
            skLineSegment(sketch, "E52.right", {"start": v(2.97, 32.62) * mm, "end": v(2.97, 27.72) * mm});
            skLineSegment(sketch, "E53", {"start": v(-3.03, 27.72) * mm, "end": v(-2.01, 26.62) * mm});
            skLineSegment(sketch, "E54", {"start": v(2.97, 27.72) * mm, "end": v(1.95, 26.62) * mm});
            skLineSegment(sketch, "E55", {"start": v(-9.23, 27.72) * mm, "end": v(-8.05, 26.62) * mm});
            skLineSegment(sketch, "E56", {"start": v(-3.23, 27.72) * mm, "end": v(-4.42, 26.62) * mm});
            skPoint(sketch, "E57.orphan", {"position": v(-9.23, 26.62) * mm});
            skPoint(sketch, "E58.orphan", {"position": v(-3.23, 26.62) * mm});
            skPoint(sketch, "E59.orphan", {"position": v(-3.03, 26.62) * mm});
            skPoint(sketch, "E60.orphan", {"position": v(2.97, 26.62) * mm});
            skSolve(sketch);
        }
        {
            var Q0;
            Q0=qSketchRegion(id+"F24",true);
            extrude(context, id + "F25", {"entities" : qUnion([Q0]), "operationType" : NewBodyOperationType.ADD, "depth" : 1.5 * mm});
        }
        {
            var Q0;
            Q0=makeQuery(id+"F25.opExtrude","CAP_FACE",FACE,{"disambiguationData":[OSD([sQuery(id+"F24.wireOp",EDGE,"E51.bottom"),sQuery(id+"F24.wireOp",EDGE,"E51.top"),sQuery(id+"F24.wireOp",EDGE,"E51.left"),sQuery(id+"F24.wireOp",EDGE,"E51.right"),sQuery(id+"F24.wireOp",EDGE,"E55"),sQuery(id+"F24.wireOp",EDGE,"E56")])],"isStart":false});
            var sketch = newSketch(context, id + "F26", { "sketchPlane" : qUnion([Q0])});
            skCircle(sketch, "E61", {"center": v(-6.23, 29.62) * mm, "radius": 3 * mm});
            skSolve(sketch);
        }
        {
            var Q0;
            Q0=makeQuery(id+"F25.opExtrude","CAP_FACE",FACE,{"disambiguationData":[OSD([sQuery(id+"F24.wireOp",EDGE,"E52.bottom"),sQuery(id+"F24.wireOp",EDGE,"E52.top"),sQuery(id+"F24.wireOp",EDGE,"E52.left"),sQuery(id+"F24.wireOp",EDGE,"E52.right"),sQuery(id+"F24.wireOp",EDGE,"E53"),sQuery(id+"F24.wireOp",EDGE,"E54")])],"isStart":false});
            var sketch = newSketch(context, id + "F27", { "sketchPlane" : qUnion([Q0])});
            skCircle(sketch, "E62", {"center": v(-0.03, 29.62) * mm, "radius": 3 * mm});
            skSolve(sketch);
        }
        {
            var Q0;
            {var subQ0=sQuery(id+"F26.wireOp",EDGE,"E61");var subQ1=makeQuery(id+"F26.imprint","INTERSECT",VERTEX,{"derivedFrom":[makeQuery(id+"F25.opExtrude","CAP_EDGE",EDGE,{"disambiguationData":[OSD([sQuery(id+"F24.wireOp",EDGE,"E51.bottom")])],"isStart":false}),subQ0]});Q0=makeQuery(id+"F26.imprint","IMPRINT",FACE,{"disambiguationData":[TD([[makeQuery(id+"F26.imprint","IMPRINT",EDGE,{"disambiguationData":[TD([[subQ1,1.0]])],"derivedFrom":subQ0}),1.0]])]});}
            var Q1;
            {var subQ0=sQuery(id+"F27.wireOp",EDGE,"E62");var subQ1=makeQuery(id+"F27.imprint","INTERSECT",VERTEX,{"derivedFrom":[makeQuery(id+"F25.opExtrude","CAP_EDGE",EDGE,{"disambiguationData":[OSD([sQuery(id+"F24.wireOp",EDGE,"E52.bottom")])],"isStart":false}),subQ0]});Q1=makeQuery(id+"F27.imprint","IMPRINT",FACE,{"disambiguationData":[TD([[makeQuery(id+"F27.imprint","IMPRINT",EDGE,{"disambiguationData":[TD([[subQ1,1.0]])],"derivedFrom":subQ0}),1.0]])]});}
            extrude(context, id + "F28", {"entities" : qUnion([Q0, Q1]), "operationType" : NewBodyOperationType.ADD, "depth" : 6.5 * mm});
        }
        {
            var Q0;
            Q0=makeQuery(id+"F25.opExtrude","SWEPT_EDGE",EDGE,{"disambiguationData":[OSD([sQuery(id+"F24.wireOp",EDGE,"E52.bottom"),sQuery(id+"F24.wireOp",EDGE,"E52.right")])]});
            var Q1;
            Q1=makeQuery(id+"F25.opExtrude","SWEPT_EDGE",EDGE,{"disambiguationData":[OSD([sQuery(id+"F24.wireOp",EDGE,"E52.bottom"),sQuery(id+"F24.wireOp",EDGE,"E52.left")])]});
            fillet(context, id + "F29", {"entities" : qUnion([Q0, Q1]), "radius" : 0.3 * mm, "tangentPropagation" : true, "allowEdgeOverflow" : false});
        }
        {
            var Q0;
            Q0=makeQuery(id+"F25.opExtrude","SWEPT_EDGE",EDGE,{"disambiguationData":[OSD([sQuery(id+"F24.wireOp",EDGE,"E51.bottom"),sQuery(id+"F24.wireOp",EDGE,"E51.right")])]});
            var Q1;
            Q1=makeQuery(id+"F25.opExtrude","SWEPT_EDGE",EDGE,{"disambiguationData":[OSD([sQuery(id+"F24.wireOp",EDGE,"E51.bottom"),sQuery(id+"F24.wireOp",EDGE,"E51.left")])]});
            fillet(context, id + "F30", {"entities" : qUnion([Q0, Q1]), "radius" : 0.1 * mm, "tangentPropagation" : true, "allowEdgeOverflow" : false});
        }
        {
            var Q0;
            {var subQ0=sQuery(id+"F4.wireOp",EDGE,"E11.left");Q0=makeQuery(id+"F4.imprint","IMPRINT",FACE,{"disambiguationData":[TD([[makeQuery(id+"F4.imprint","IMPRINT",EDGE,{"derivedFrom":subQ0}),-1.0]])]});}
            var sketch = newSketch(context, id + "F31", { "sketchPlane" : qUnion([Q0])});
            skLineSegment(sketch, "E63.bottom", {"start": v(-35.83, 10.62) * mm, "end": v(-29.83, 10.62) * mm});
            skLineSegment(sketch, "E63.top", {"start": v(-35.83, 4.62) * mm, "end": v(-29.83, 4.62) * mm});
            skLineSegment(sketch, "E63.left", {"start": v(-35.83, 10.62) * mm, "end": v(-35.83, 4.62) * mm});
            skLineSegment(sketch, "E63.right", {"start": v(-29.83, 10.62) * mm, "end": v(-29.83, 4.62) * mm});
            skCircle(sketch, "E64", {"center": v(-32.83, 7.62) * mm, "radius": 2 * mm});
            skPoint(sketch, "E64.centerSnap0", {"position": v(-29.83, 7.62) * mm});
            skPoint(sketch, "E64.centerSnap1", {"position": v(-32.83, 10.62) * mm});
            skCircle(sketch, "E65", {"center": v(-35.06, 9.9) * mm, "radius": 0.5 * mm});
            skCircle(sketch, "E66.1.0", {"center": v(-35.1, 5.4) * mm, "radius": 0.5 * mm});
            skCircle(sketch, "E66.2.0", {"center": v(-30.6, 5.35) * mm, "radius": 0.5 * mm});
            skCircle(sketch, "E67.1.3.0", {"center": v(-30.56, 9.85) * mm, "radius": 0.5 * mm});
            skSolve(sketch);
        }
        {
            var Q0;
            Q0=makeQuery(id+"F19.opExtrude","CAP_FACE",FACE,{"disambiguationData":[OSD([sQuery(id+"F9.wireOp",EDGE,"E43.bottom"),sQuery(id+"F9.wireOp",EDGE,"E43.top"),sQuery(id+"F9.wireOp",EDGE,"E43.left"),sQuery(id+"F9.wireOp",EDGE,"E43.right")])],"isStart":false});
            var sketch = newSketch(context, id + "F32", { "sketchPlane" : qUnion([Q0])});
            skLineSegment(sketch, "E68.bottom", {"start": v(-24.56, 33.2) * mm, "end": v(-23.26, 33.2) * mm});
            skLineSegment(sketch, "E68.top", {"start": v(-24.56, 31.9) * mm, "end": v(-23.26, 31.9) * mm});
            skLineSegment(sketch, "E68.left", {"start": v(-24.56, 33.2) * mm, "end": v(-24.56, 31.9) * mm});
            skLineSegment(sketch, "E68.right", {"start": v(-23.26, 33.2) * mm, "end": v(-23.26, 31.9) * mm});
            skLineSegment(sketch, "E69.bottom", {"start": v(-22.08, 33.23) * mm, "end": v(-20.75, 33.23) * mm});
            skLineSegment(sketch, "E69.top", {"start": v(-22.08, 31.92) * mm, "end": v(-20.75, 31.92) * mm});
            skLineSegment(sketch, "E69.left", {"start": v(-22.08, 33.23) * mm, "end": v(-22.08, 31.92) * mm});
            skLineSegment(sketch, "E69.right", {"start": v(-20.75, 33.23) * mm, "end": v(-20.75, 31.92) * mm});
            skLineSegment(sketch, "E70.bottom", {"start": v(-19.58, 33.23) * mm, "end": v(-18.2, 33.23) * mm});
            skLineSegment(sketch, "E70.top", {"start": v(-19.58, 31.92) * mm, "end": v(-18.2, 31.92) * mm});
            skLineSegment(sketch, "E70.left", {"start": v(-19.58, 33.23) * mm, "end": v(-19.58, 31.92) * mm});
            skLineSegment(sketch, "E70.right", {"start": v(-18.2, 33.23) * mm, "end": v(-18.2, 31.92) * mm});
            skLineSegment(sketch, "E71.bottom", {"start": v(-17.1, 33.2) * mm, "end": v(-15.7, 33.2) * mm});
            skLineSegment(sketch, "E71.top", {"start": v(-17.1, 31.87) * mm, "end": v(-15.7, 31.87) * mm});
            skLineSegment(sketch, "E71.left", {"start": v(-17.1, 33.2) * mm, "end": v(-17.1, 31.87) * mm});
            skLineSegment(sketch, "E71.right", {"start": v(-15.7, 33.2) * mm, "end": v(-15.7, 31.87) * mm});
            skLineSegment(sketch, "E72.bottom", {"start": v(-14.58, 33.2) * mm, "end": v(-13.19, 33.2) * mm});
            skLineSegment(sketch, "E72.top", {"start": v(-14.58, 31.9) * mm, "end": v(-13.19, 31.9) * mm});
            skLineSegment(sketch, "E72.left", {"start": v(-14.58, 33.2) * mm, "end": v(-14.58, 31.9) * mm});
            skLineSegment(sketch, "E72.right", {"start": v(-13.19, 33.2) * mm, "end": v(-13.19, 31.9) * mm});
            skLineSegment(sketch, "E73.bottom", {"start": v(-12.11, 33.2) * mm, "end": v(-10.7, 33.2) * mm});
            skLineSegment(sketch, "E73.top", {"start": v(-12.11, 31.92) * mm, "end": v(-10.7, 31.92) * mm});
            skLineSegment(sketch, "E73.left", {"start": v(-12.11, 33.2) * mm, "end": v(-12.11, 31.92) * mm});
            skLineSegment(sketch, "E73.right", {"start": v(-10.7, 33.2) * mm, "end": v(-10.7, 31.92) * mm});
            skSolve(sketch);
        }
        {
            var Q0;
            Q0=makeQuery(id+"F32.imprint","IMPRINT",FACE,{"disambiguationData":[TD([[makeQuery(id+"F32.imprint","IMPRINT",EDGE,{"derivedFrom":sQuery(id+"F32.wireOp",EDGE,"E68.bottom")}),-1.0]])]});
            var Q1;
            Q1=makeQuery(id+"F32.imprint","IMPRINT",FACE,{"disambiguationData":[TD([[makeQuery(id+"F32.imprint","IMPRINT",EDGE,{"derivedFrom":sQuery(id+"F32.wireOp",EDGE,"E69.bottom")}),-1.0]])]});
            var Q2;
            Q2=makeQuery(id+"F32.imprint","IMPRINT",FACE,{"disambiguationData":[TD([[makeQuery(id+"F32.imprint","IMPRINT",EDGE,{"derivedFrom":sQuery(id+"F32.wireOp",EDGE,"E71.bottom")}),-1.0]])]});
            var Q3;
            Q3=makeQuery(id+"F32.imprint","IMPRINT",FACE,{"disambiguationData":[TD([[makeQuery(id+"F32.imprint","IMPRINT",EDGE,{"derivedFrom":sQuery(id+"F32.wireOp",EDGE,"E70.bottom")}),-1.0]])]});
            var Q4;
            Q4=makeQuery(id+"F32.imprint","IMPRINT",FACE,{"disambiguationData":[TD([[makeQuery(id+"F32.imprint","IMPRINT",EDGE,{"derivedFrom":sQuery(id+"F32.wireOp",EDGE,"E72.bottom")}),-1.0]])]});
            var Q5;
            Q5=makeQuery(id+"F32.imprint","IMPRINT",FACE,{"disambiguationData":[TD([[makeQuery(id+"F32.imprint","IMPRINT",EDGE,{"derivedFrom":sQuery(id+"F32.wireOp",EDGE,"E73.bottom")}),-1.0]])]});
            extrude(context, id + "F33", {"entities" : qUnion([Q0, Q1, Q2, Q3, Q4, Q5]), "operationType" : NewBodyOperationType.REMOVE, "oppositeDirection" : true, "depth" : 8 * mm});
        }
        {
            var Q0;
            Q0=makeQuery(id+"F19.opExtrude","CAP_FACE",FACE,{"disambiguationData":[OSD([sQuery(id+"F9.wireOp",EDGE,"E44.bottom"),sQuery(id+"F9.wireOp",EDGE,"E44.top"),sQuery(id+"F9.wireOp",EDGE,"E44.left"),sQuery(id+"F9.wireOp",EDGE,"E44.right")])],"isStart":false});
            var sketch = newSketch(context, id + "F34", { "sketchPlane" : qUnion([Q0])});
            skLineSegment(sketch, "E74.bottom", {"start": v(-42.09, -15.77) * mm, "end": v(-40.7, -15.77) * mm});
            skLineSegment(sketch, "E74.top", {"start": v(-42.09, -17.09) * mm, "end": v(-40.7, -17.09) * mm});
            skLineSegment(sketch, "E74.left", {"start": v(-42.09, -15.77) * mm, "end": v(-42.09, -17.09) * mm});
            skLineSegment(sketch, "E74.right", {"start": v(-40.7, -15.77) * mm, "end": v(-40.7, -17.09) * mm});
            skLineSegment(sketch, "E75.bottom", {"start": v(-39.55, -15.77) * mm, "end": v(-38.25, -15.77) * mm});
            skLineSegment(sketch, "E75.top", {"start": v(-39.55, -17.08) * mm, "end": v(-38.25, -17.08) * mm});
            skLineSegment(sketch, "E75.left", {"start": v(-39.55, -15.77) * mm, "end": v(-39.55, -17.08) * mm});
            skLineSegment(sketch, "E75.right", {"start": v(-38.25, -15.77) * mm, "end": v(-38.25, -17.08) * mm});
            skLineSegment(sketch, "E76.bottom", {"start": v(-37.05, -15.77) * mm, "end": v(-35.76, -15.77) * mm});
            skLineSegment(sketch, "E76.top", {"start": v(-37.05, -17.08) * mm, "end": v(-35.76, -17.08) * mm});
            skLineSegment(sketch, "E76.left", {"start": v(-37.05, -15.77) * mm, "end": v(-37.05, -17.08) * mm});
            skLineSegment(sketch, "E76.right", {"start": v(-35.76, -15.77) * mm, "end": v(-35.76, -17.08) * mm});
            skLineSegment(sketch, "E77.bottom", {"start": v(-34.58, -15.77) * mm, "end": v(-33.27, -15.77) * mm});
            skLineSegment(sketch, "E77.top", {"start": v(-34.58, -17.08) * mm, "end": v(-33.27, -17.08) * mm});
            skLineSegment(sketch, "E77.left", {"start": v(-34.58, -15.77) * mm, "end": v(-34.58, -17.08) * mm});
            skLineSegment(sketch, "E77.right", {"start": v(-33.27, -15.77) * mm, "end": v(-33.27, -17.08) * mm});
            skLineSegment(sketch, "E78.bottom", {"start": v(-32.08, -15.77) * mm, "end": v(-30.79, -15.77) * mm});
            skLineSegment(sketch, "E78.top", {"start": v(-32.08, -17.08) * mm, "end": v(-30.79, -17.08) * mm});
            skLineSegment(sketch, "E78.left", {"start": v(-32.08, -15.77) * mm, "end": v(-32.08, -17.08) * mm});
            skLineSegment(sketch, "E78.right", {"start": v(-30.79, -15.77) * mm, "end": v(-30.79, -17.08) * mm});
            skLineSegment(sketch, "E79.bottom", {"start": v(-29.56, -15.77) * mm, "end": v(-28.26, -15.77) * mm});
            skLineSegment(sketch, "E79.top", {"start": v(-29.56, -17.09) * mm, "end": v(-28.26, -17.09) * mm});
            skLineSegment(sketch, "E79.left", {"start": v(-29.56, -15.77) * mm, "end": v(-29.56, -17.09) * mm});
            skLineSegment(sketch, "E79.right", {"start": v(-28.26, -15.77) * mm, "end": v(-28.26, -17.09) * mm});
            skLineSegment(sketch, "E80.bottom", {"start": v(-27.1, -15.77) * mm, "end": v(-25.8, -15.77) * mm});
            skLineSegment(sketch, "E80.top", {"start": v(-27.1, -17.12) * mm, "end": v(-25.8, -17.12) * mm});
            skLineSegment(sketch, "E80.left", {"start": v(-27.1, -15.77) * mm, "end": v(-27.1, -17.12) * mm});
            skLineSegment(sketch, "E80.right", {"start": v(-25.8, -15.77) * mm, "end": v(-25.8, -17.12) * mm});
            skLineSegment(sketch, "E81.bottom", {"start": v(-24.68, -15.79) * mm, "end": v(-23.3, -15.79) * mm});
            skLineSegment(sketch, "E81.top", {"start": v(-24.68, -17.12) * mm, "end": v(-23.3, -17.12) * mm});
            skLineSegment(sketch, "E81.left", {"start": v(-24.68, -15.79) * mm, "end": v(-24.68, -17.12) * mm});
            skLineSegment(sketch, "E81.right", {"start": v(-23.3, -15.79) * mm, "end": v(-23.3, -17.12) * mm});
            skSolve(sketch);
        }
        {
            var Q0;
            Q0=makeQuery(id+"F34.imprint","IMPRINT",FACE,{"disambiguationData":[TD([[makeQuery(id+"F34.imprint","IMPRINT",EDGE,{"derivedFrom":sQuery(id+"F34.wireOp",EDGE,"E74.bottom")}),-1.0]])]});
            var Q1;
            Q1=makeQuery(id+"F34.imprint","IMPRINT",FACE,{"disambiguationData":[TD([[makeQuery(id+"F34.imprint","IMPRINT",EDGE,{"derivedFrom":sQuery(id+"F34.wireOp",EDGE,"E75.bottom")}),-1.0]])]});
            var Q2;
            Q2=makeQuery(id+"F34.imprint","IMPRINT",FACE,{"disambiguationData":[TD([[makeQuery(id+"F34.imprint","IMPRINT",EDGE,{"derivedFrom":sQuery(id+"F34.wireOp",EDGE,"E76.bottom")}),-1.0]])]});
            var Q3;
            Q3=makeQuery(id+"F34.imprint","IMPRINT",FACE,{"disambiguationData":[TD([[makeQuery(id+"F34.imprint","IMPRINT",EDGE,{"derivedFrom":sQuery(id+"F34.wireOp",EDGE,"E77.bottom")}),-1.0]])]});
            var Q4;
            Q4=makeQuery(id+"F34.imprint","IMPRINT",FACE,{"disambiguationData":[TD([[makeQuery(id+"F34.imprint","IMPRINT",EDGE,{"derivedFrom":sQuery(id+"F34.wireOp",EDGE,"E78.bottom")}),-1.0]])]});
            var Q5;
            Q5=makeQuery(id+"F34.imprint","IMPRINT",FACE,{"disambiguationData":[TD([[makeQuery(id+"F34.imprint","IMPRINT",EDGE,{"derivedFrom":sQuery(id+"F34.wireOp",EDGE,"E79.bottom")}),-1.0]])]});
            var Q6;
            Q6=makeQuery(id+"F34.imprint","IMPRINT",FACE,{"disambiguationData":[TD([[makeQuery(id+"F34.imprint","IMPRINT",EDGE,{"derivedFrom":sQuery(id+"F34.wireOp",EDGE,"E80.bottom")}),-1.0]])]});
            var Q7;
            Q7=makeQuery(id+"F34.imprint","IMPRINT",FACE,{"disambiguationData":[TD([[makeQuery(id+"F34.imprint","IMPRINT",EDGE,{"derivedFrom":sQuery(id+"F34.wireOp",EDGE,"E81.bottom")}),-1.0]])]});
            extrude(context, id + "F35", {"entities" : qUnion([Q0, Q1, Q2, Q3, Q4, Q5, Q6, Q7]), "operationType" : NewBodyOperationType.REMOVE, "oppositeDirection" : true, "depth" : 8 * mm});
        }
        {
            var Q0;
            Q0=makeQuery(id+"F31.imprint","IMPRINT",FACE,{"disambiguationData":[TD([[makeQuery(id+"F31.imprint","IMPRINT",EDGE,{"derivedFrom":sQuery(id+"F31.wireOp",EDGE,"E64")}),1.0]])]});
            extrude(context, id + "F36", {"entities" : qUnion([Q0]), "operationType" : NewBodyOperationType.ADD, "depth" : 4 * mm});
        }
        {
            var Q0;
            Q0=makeQuery(id+"F31.imprint","IMPRINT",FACE,{"disambiguationData":[TD([[makeQuery(id+"F31.imprint","IMPRINT",EDGE,{"derivedFrom":sQuery(id+"F31.wireOp",EDGE,"E63.bottom")}),-1.0]])]});
            var Q1;
            Q1=sQuery(id+"F31.wireOp",EDGE,"E63.left");
            var Q2;
            Q2=sQuery(id+"F31.wireOp",EDGE,"E63.top");
            var Q3;
            Q3=sQuery(id+"F31.wireOp",EDGE,"E63.right");
            var Q4;
            Q4=sQuery(id+"F31.wireOp",EDGE,"E63.bottom");
            extrude(context, id + "F37", {"entities" : qUnion([Q0]), "operationType" : NewBodyOperationType.ADD, "surfaceEntities" : qUnion([Q1, Q2, Q3, Q4]), "depth" : 3 * mm});
        }
        {
            var Q0;
            Q0=makeQuery(id+"F37.opExtrude","CAP_FACE",FACE,{"disambiguationData":[OSD([sQuery(id+"F31.wireOp",EDGE,"E63.bottom"),sQuery(id+"F31.wireOp",EDGE,"E63.top"),sQuery(id+"F31.wireOp",EDGE,"E63.left"),sQuery(id+"F31.wireOp",EDGE,"E63.right"),sQuery(id+"F31.wireOp",EDGE,"E64"),sQuery(id+"F31.wireOp",EDGE,"E65"),sQuery(id+"F31.wireOp",EDGE,"E66.1.0"),sQuery(id+"F31.wireOp",EDGE,"E66.2.0"),sQuery(id+"F31.wireOp",EDGE,"E67.1.3.0")])],"isStart":false});
            var sketch = newSketch(context, id + "F38", { "sketchPlane" : qUnion([Q0])});
            skCircle(sketch, "E82", {"center": v(-30.6, 5.35) * mm, "radius": 0.49 * mm});
            skCircle(sketch, "E83", {"center": v(-30.56, 9.85) * mm, "radius": 0.48 * mm});
            skCircle(sketch, "E84", {"center": v(-35.06, 9.9) * mm, "radius": 0.48 * mm});
            skCircle(sketch, "E85", {"center": v(-35.1, 5.4) * mm, "radius": 0.5 * mm});
            skSolve(sketch);
        }
        {
            var Q0;
            Q0=makeQuery(id+"F38.imprint","IMPRINT",FACE,{"disambiguationData":[TD([[makeQuery(id+"F38.imprint","IMPRINT",EDGE,{"derivedFrom":sQuery(id+"F38.wireOp",EDGE,"E83")}),1.0]])]});
            var Q1;
            Q1=makeQuery(id+"F38.imprint","IMPRINT",FACE,{"disambiguationData":[TD([[makeQuery(id+"F38.imprint","IMPRINT",EDGE,{"derivedFrom":sQuery(id+"F38.wireOp",EDGE,"E84")}),1.0]])]});
            var Q2;
            Q2=makeQuery(id+"F38.imprint","IMPRINT",FACE,{"disambiguationData":[TD([[makeQuery(id+"F38.imprint","IMPRINT",EDGE,{"derivedFrom":sQuery(id+"F38.wireOp",EDGE,"E85")}),1.0]])]});
            var Q3;
            Q3=makeQuery(id+"F38.imprint","IMPRINT",FACE,{"disambiguationData":[TD([[makeQuery(id+"F38.imprint","IMPRINT",EDGE,{"derivedFrom":sQuery(id+"F38.wireOp",EDGE,"E82")}),1.0]])]});
            extrude(context, id + "F39", {"entities" : qUnion([Q0, Q1, Q2, Q3]), "operationType" : NewBodyOperationType.ADD, "depth" : 0.1 * mm});
        }
        {
            var Q0;
            Q0=makeQuery(id+"F9.imprint","IMPRINT",FACE,{"disambiguationData":[TD([[makeQuery(id+"F9.imprint","IMPRINT",EDGE,{"derivedFrom":sQuery(id+"F9.wireOp",EDGE,"E42.bottom")}),1.0]])]});
            var sketch = newSketch(context, id + "F40", { "sketchPlane" : qUnion([Q0])});
            skLineSegment(sketch, "E86.bottom", {"start": v(10.97, 30.02) * mm, "end": v(22.17, 30.02) * mm});
            skLineSegment(sketch, "E86.top", {"start": v(10.97, 21.32) * mm, "end": v(22.17, 21.32) * mm});
            skLineSegment(sketch, "E86.left", {"start": v(10.97, 30.02) * mm, "end": v(10.97, 21.32) * mm});
            skLineSegment(sketch, "E86.right", {"start": v(22.17, 30.02) * mm, "end": v(22.17, 21.32) * mm});
            skSolve(sketch);
        }
        {
            var Q0;
            Q0=makeQuery(id+"F9.imprint","IMPRINT",FACE,{"disambiguationData":[TD([[makeQuery(id+"F9.imprint","IMPRINT",EDGE,{"derivedFrom":sQuery(id+"F9.wireOp",EDGE,"E42.bottom")}),1.0]])]});
            var sketch = newSketch(context, id + "F41", { "sketchPlane" : qUnion([Q0])});
            skLineSegment(sketch, "E87.bottom", {"start": v(10.96, 30.02) * mm, "end": v(22.15, 30.02) * mm});
            skLineSegment(sketch, "E87.top", {"start": v(10.96, 21.33) * mm, "end": v(22.15, 21.33) * mm});
            skLineSegment(sketch, "E87.left", {"start": v(10.96, 30.02) * mm, "end": v(10.96, 21.33) * mm});
            skLineSegment(sketch, "E87.right", {"start": v(22.15, 30.02) * mm, "end": v(22.15, 21.33) * mm});
            skSolve(sketch);
        }
        {
            var Q0;
            Q0=makeQuery(id+"F40.imprint","IMPRINT",FACE,{"disambiguationData":[TD([[makeQuery(id+"F40.imprint","IMPRINT",EDGE,{"derivedFrom":sQuery(id+"F40.wireOp",EDGE,"E86.bottom")}),-1.0]])]});
            var Q1;
            Q1=sQuery(id+"F41.wireOp",EDGE,"E87.bottom");
            var Q2;
            Q2=sQuery(id+"F41.wireOp",EDGE,"E87.left");
            var Q3;
            Q3=sQuery(id+"F41.wireOp",EDGE,"E87.top");
            var Q4;
            Q4=sQuery(id+"F41.wireOp",EDGE,"E87.right");
            extrude(context, id + "F42", {"entities" : qUnion([Q0]), "operationType" : NewBodyOperationType.ADD, "surfaceEntities" : qUnion([Q1, Q2, Q3, Q4]), "depth" : 10.1 * mm});
        }
        {
            var Q0;
            Q0=makeQuery(id+"F42.opExtrude","SWEPT_FACE",FACE,{"disambiguationData":[OSD([sQuery(id+"F40.wireOp",EDGE,"E86.left")])]});
            var sketch = newSketch(context, id + "F43", { "sketchPlane" : qUnion([Q0])});
            skArc(sketch, "E88", {"start": v(-21.32, 6.1) * mm, "mid": v(-25.67, 11.1) * mm, "end": v(-30.02, 6.1) * mm});
            skSolve(sketch);
        }
        {
            var Q0;
            {var subQ0=sQuery(id+"F43.wireOp",EDGE,"E88");var subQ1=sQuery(id+"F40.wireOp",EDGE,"E86.left");var subQ2=makeQuery(id+"F42.opExtrude","CAP_EDGE",EDGE,{"disambiguationData":[OSD([subQ1])],"isStart":false});var subQ3=makeQuery(id+"F43.imprint","INTERSECT",VERTEX,{"derivedFrom":[subQ2,subQ0]});Q0=makeQuery(id+"F43.imprint","IMPRINT",FACE,{"disambiguationData":[TD([[makeQuery(id+"F43.imprint","IMPRINT",EDGE,{"disambiguationData":[TD([[subQ3,-1.0]])],"derivedFrom":subQ0}),-1.0]])]});}
            var Q1;
            {var subQ0=sQuery(id+"F43.wireOp",EDGE,"E88");var subQ1=sQuery(id+"F40.wireOp",EDGE,"E86.left");var subQ4=makeQuery(id+"F42.opExtrude","CAP_EDGE",EDGE,{"disambiguationData":[OSD([subQ1])],"isStart":false});var subQ5=makeQuery(id+"F43.imprint","INTERSECT",VERTEX,{"derivedFrom":[subQ4,subQ0]});Q1=makeQuery(id+"F43.imprint","IMPRINT",FACE,{"disambiguationData":[TD([[makeQuery(id+"F43.imprint","IMPRINT",EDGE,{"disambiguationData":[TD([[subQ5,1.0]])],"derivedFrom":subQ0}),-1.0]])]});}
            extrude(context, id + "F44", {"entities" : qUnion([Q0, Q1]), "operationType" : NewBodyOperationType.REMOVE, "oppositeDirection" : true, "depth" : 25.4 * mm});
        }
        {
            var Q0;
            Q0=makeQuery(id+"F42.boolean.opBoolean","MERGE",FACE,{"derivedFrom":[makeQuery(id+"F1.opExtrude","SWEPT_FACE",FACE,{"disambiguationData":[OSD([sQuery(id+"F0.wireOp",EDGE,"E0.right")])]}),makeQuery(id+"F42.opExtrude","SWEPT_FACE",FACE,{"disambiguationData":[OSD([sQuery(id+"F40.wireOp",EDGE,"E86.right")])]})]});
            var sketch = newSketch(context, id + "F45", { "sketchPlane" : qUnion([Q0])});
            skLineSegment(sketch, "E89.bottom", {"start": v(20.82, 12) * mm, "end": v(30.52, 12) * mm});
            skLineSegment(sketch, "E89.top", {"start": v(20.82, 1) * mm, "end": v(30.52, 1) * mm});
            skLineSegment(sketch, "E89.left", {"start": v(20.82, 12) * mm, "end": v(20.82, 1) * mm});
            skLineSegment(sketch, "E89.right", {"start": v(30.52, 12) * mm, "end": v(30.52, 1) * mm});
            skSolve(sketch);
        }
        {
            var Q0;
            Q0=makeQuery(id+"F45.imprint","IMPRINT",FACE,{"disambiguationData":[TD([[makeQuery(id+"F45.imprint","IMPRINT",EDGE,{"derivedFrom":sQuery(id+"F45.wireOp",EDGE,"E89.bottom")}),-1.0]])]});
            var Q1;
            {var subQ1=sQuery(id+"F40.wireOp",EDGE,"E86.right");var subQ2=sQuery(id+"F40.wireOp",EDGE,"E86.bottom");var subQ3=sQuery(id+"F0.wireOp",EDGE,"E0.right");var subQ4=makeQuery(id+"F42.opExtrude","SWEPT_EDGE",EDGE,{"disambiguationData":[OSD([subQ3,subQ2,subQ1])]});Q1=makeQuery(id+"F45.imprint","IMPRINT",FACE,{"disambiguationData":[TD([[makeQuery(id+"F45.imprint","IMPRINT",EDGE,{"derivedFrom":subQ4}),-1.0]])]});}
            extrude(context, id + "F46", {"entities" : qUnion([Q0, Q1]), "depth" : 3 * mm});
        }
        {
            var Q0;
            Q0=makeQuery(id+"F46.opExtrude","CAP_FACE",FACE,{"disambiguationData":[OSD([sQuery(id+"F45.wireOp",EDGE,"E89.bottom"),sQuery(id+"F45.wireOp",EDGE,"E89.top"),sQuery(id+"F45.wireOp",EDGE,"E89.left"),sQuery(id+"F45.wireOp",EDGE,"E89.right")])],"isStart":false});
            var sketch = newSketch(context, id + "F47", { "sketchPlane" : qUnion([Q0])});
            skCircle(sketch, "E90", {"center": v(25.67, 8) * mm, "radius": 3 * mm});
            skSolve(sketch);
        }
        {
            var Q0;
            Q0=makeQuery(id+"F47.imprint","IMPRINT",FACE,{"disambiguationData":[TD([[makeQuery(id+"F47.imprint","IMPRINT",EDGE,{"derivedFrom":sQuery(id+"F47.wireOp",EDGE,"E90")}),1.0]])]});
            extrude(context, id + "F48", {"entities" : qUnion([Q0]), "operationType" : NewBodyOperationType.REMOVE, "oppositeDirection" : true, "depth" : 11 * mm});
        }
        {
            var Q0;
            Q0=makeQuery(id+"F42.boolean.opBoolean","MERGE",FACE,{"derivedFrom":[makeQuery(id+"F1.opExtrude","SWEPT_FACE",FACE,{"disambiguationData":[OSD([sQuery(id+"F0.wireOp",EDGE,"E0.right")])]}),makeQuery(id+"F42.opExtrude","SWEPT_FACE",FACE,{"disambiguationData":[OSD([sQuery(id+"F40.wireOp",EDGE,"E86.right")])]})]});
            var sketch = newSketch(context, id + "F49", { "sketchPlane" : qUnion([Q0])});
            skCircle(sketch, "E91", {"center": v(25.67, 8) * mm, "radius": 0.5 * mm});
            skSolve(sketch);
        }
        {
            var Q0;
            Q0=makeQuery(id+"F49.imprint","IMPRINT",FACE,{"disambiguationData":[TD([[makeQuery(id+"F49.imprint","IMPRINT",EDGE,{"derivedFrom":sQuery(id+"F49.wireOp",EDGE,"E91")}),1.0]])]});
            extrude(context, id + "F50", {"entities" : qUnion([Q0]), "operationType" : NewBodyOperationType.ADD, "depth" : 2 * mm});
        }
        {
            var Q0;
            Q0=makeQuery(id+"F46.opExtrude","CAP_FACE",FACE,{"disambiguationData":[OSD([sQuery(id+"F45.wireOp",EDGE,"E89.bottom"),sQuery(id+"F45.wireOp",EDGE,"E89.top"),sQuery(id+"F45.wireOp",EDGE,"E89.left"),sQuery(id+"F45.wireOp",EDGE,"E89.right")])],"isStart":true});
            var sketch = newSketch(context, id + "F51", { "sketchPlane" : qUnion([Q0])});
            skLineSegment(sketch, "E92.bottom", {"start": v(-21.32, 7.3) * mm, "end": v(-20.82, 7.3) * mm});
            skLineSegment(sketch, "E92.top", {"start": v(-21.32, 1) * mm, "end": v(-20.82, 1) * mm});
            skLineSegment(sketch, "E92.left", {"start": v(-21.32, 7.3) * mm, "end": v(-21.32, 1) * mm});
            skLineSegment(sketch, "E92.right", {"start": v(-20.82, 7.3) * mm, "end": v(-20.82, 1) * mm});
            skLineSegment(sketch, "E93.bottom", {"start": v(-30.52, 7.32) * mm, "end": v(-30.02, 7.32) * mm});
            skLineSegment(sketch, "E93.top", {"start": v(-30.52, 1) * mm, "end": v(-30.02, 1) * mm});
            skLineSegment(sketch, "E93.left", {"start": v(-30.52, 7.32) * mm, "end": v(-30.52, 1) * mm});
            skLineSegment(sketch, "E93.right", {"start": v(-30.02, 7.32) * mm, "end": v(-30.02, 1) * mm});
            skSolve(sketch);
        }
        {
            var Q0;
            Q0=makeQuery(id+"F51.imprint","IMPRINT",FACE,{"disambiguationData":[TD([[makeQuery(id+"F51.imprint","IMPRINT",EDGE,{"derivedFrom":sQuery(id+"F51.wireOp",EDGE,"E92.bottom")}),-1.0]])]});
            var Q1;
            Q1=makeQuery(id+"F51.imprint","IMPRINT",FACE,{"disambiguationData":[TD([[makeQuery(id+"F51.imprint","IMPRINT",EDGE,{"derivedFrom":sQuery(id+"F51.wireOp",EDGE,"E93.bottom")}),-1.0]])]});
            extrude(context, id + "F52", {"entities" : qUnion([Q0, Q1]), "depth" : 11.2 * mm});
        }
    });